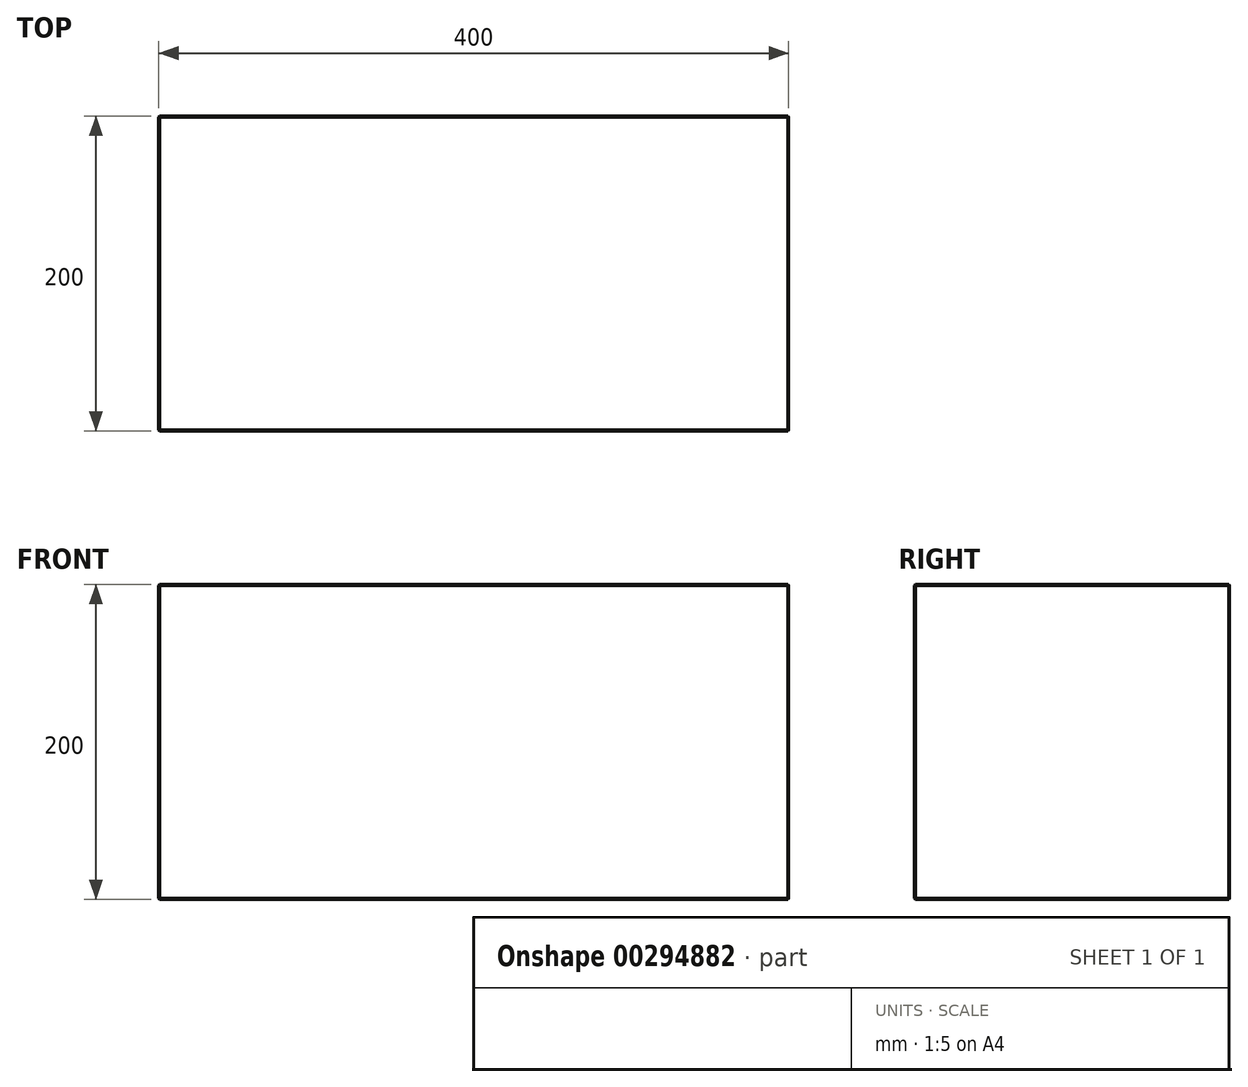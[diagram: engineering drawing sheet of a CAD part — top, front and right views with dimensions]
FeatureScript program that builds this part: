
annotation { "Feature Type Name" : "Feature", "Feature Type Description" : "" }
export const myFeature = defineFeature(function(context is Context, id is Id, definition is map)
    precondition{}
    {
        {
            var Q0;
            Q0=qCreatedBy(makeId("Top.planeOp"),FACE);
            var sketch = newSketch(context, id + "F0", { "sketchPlane" : qUnion([Q0])});
            skLineSegment(sketch, "E0.bottom", {"start": v(200, -100) * mm, "end": v(-200, -100) * mm});
            skLineSegment(sketch, "E0.top", {"start": v(200, 100) * mm, "end": v(-200, 100) * mm});
            skLineSegment(sketch, "E0.left", {"start": v(200, -100) * mm, "end": v(200, 100) * mm});
            skLineSegment(sketch, "E0.right", {"start": v(-200, -100) * mm, "end": v(-200, 100) * mm});
            skPoint(sketch, "E0.middle", {"position": v(0, 0) * mm});
            skSolve(sketch);
        }
        {
            var Q0;
            Q0=makeQuery(id+"F0.imprint","IMPRINT",FACE,{"disambiguationData":[TD([[makeQuery(id+"F0.imprint","IMPRINT",EDGE,{"derivedFrom":sQuery(id+"F0.wireOp",EDGE,"E0.bottom")}),-1.0]])]});
            extrude(context, id + "F1", {"entities" : qUnion([Q0]), "depth" : 200 * mm});
        }
        {
            var Q0;
            Q0=makeQuery(id+"F1.opExtrude","CAP_FACE",FACE,{"disambiguationData":[OSD([sQuery(id+"F0.wireOp",EDGE,"E0.bottom"),sQuery(id+"F0.wireOp",EDGE,"E0.top"),sQuery(id+"F0.wireOp",EDGE,"E0.left"),sQuery(id+"F0.wireOp",EDGE,"E0.right")])],"isStart":false});
            var Q1;
            Q1=makeQuery(id+"F1.opExtrude","SWEPT_FACE",FACE,{"disambiguationData":[OSD([sQuery(id+"F0.wireOp",EDGE,"E0.bottom")])]});
            var Q2;
            Q2=makeQuery(id+"F1.opExtrude","SWEPT_FACE",FACE,{"disambiguationData":[OSD([sQuery(id+"F0.wireOp",EDGE,"E0.left")])]});
            var Q3;
            Q3=makeQuery(id+"F1.opExtrude","SWEPT_FACE",FACE,{"disambiguationData":[OSD([sQuery(id+"F0.wireOp",EDGE,"E0.top")])]});
            var Q4;
            Q4=makeQuery(id+"F1.opExtrude","CAP_FACE",FACE,{"disambiguationData":[OSD([sQuery(id+"F0.wireOp",EDGE,"E0.bottom"),sQuery(id+"F0.wireOp",EDGE,"E0.top"),sQuery(id+"F0.wireOp",EDGE,"E0.left"),sQuery(id+"F0.wireOp",EDGE,"E0.right")])],"isStart":true});
            var Q5;
            Q5=makeQuery(id+"F1.opExtrude","SWEPT_FACE",FACE,{"disambiguationData":[OSD([sQuery(id+"F0.wireOp",EDGE,"E0.right")])]});
            chamfer(context, id + "F2", {"entities" : qUnion([Q0, Q1, Q2, Q3, Q4, Q5]), "width" : 0.5 * mm, "tangentPropagation" : true});
        }
    });
